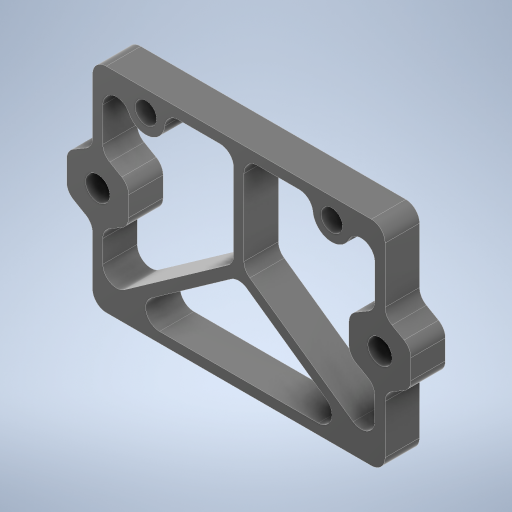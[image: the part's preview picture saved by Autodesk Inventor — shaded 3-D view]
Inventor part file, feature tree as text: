
AUTODESK INVENTOR PART (.ipt)
format: ipt  version: 2024.2 (Build 282272000, 272)  size: 388,608 bytes
history: native  units: mm
features: hole x2, fillet x2, other x1, mirror x1
ambient origin geometry x8: Origin, YZ Plane, XZ Plane, XY Plane, X Axis, Y Axis, Z Axis, Center Point
bodies: Solid2 (feature_tree)
feature tree (6):
  other  "LegBaseBackFulcrumFrame.ipt"
  hole  "Hole3"  [1 undecoded]
  hole  "Hole4"  [1 undecoded]
  fillet  "Fillet1"  Radius=5.0mm
  mirror  "Mirror2"
  fillet  "Fillet2"  Radius=2.0mm
note: 2 required parameter values undecoded (feature->parameter linkage not recoverable at this tier; creation-order binding heuristic only, values carry confidence <= 0.55)
